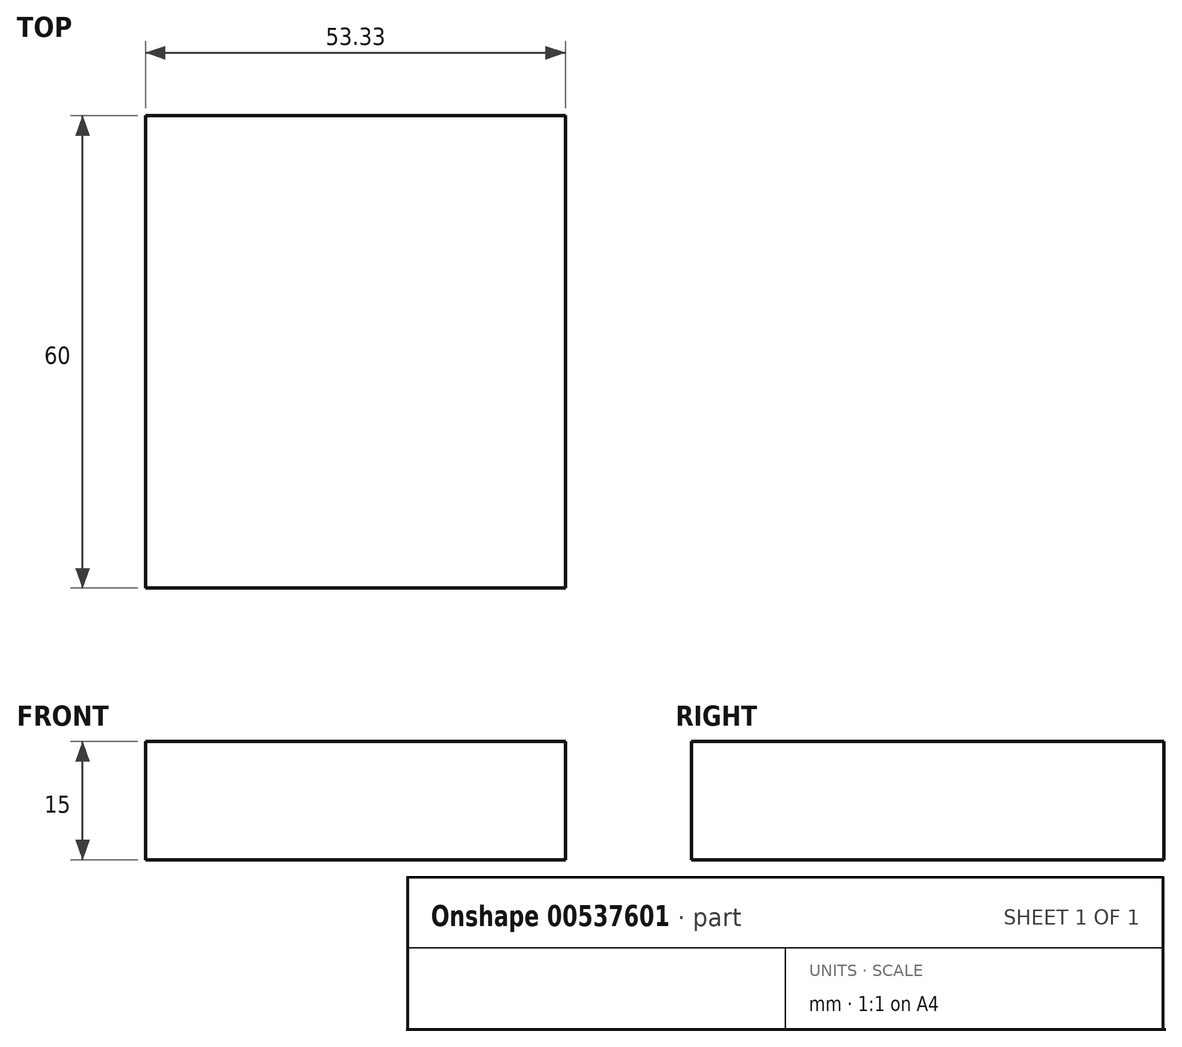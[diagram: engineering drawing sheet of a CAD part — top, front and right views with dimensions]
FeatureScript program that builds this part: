
annotation { "Feature Type Name" : "Feature", "Feature Type Description" : "" }
export const myFeature = defineFeature(function(context is Context, id is Id, definition is map)
    precondition{}
    {
        {
            var Q0;
            Q0=qCreatedBy(makeId("Top.planeOp"),FACE);
            var sketch = newSketch(context, id + "F0", { "sketchPlane" : qUnion([Q0])});
            skLineSegment(sketch, "E0.bottom", {"start": v(0, 0) * mm, "end": v(53.33, 0) * mm});
            skLineSegment(sketch, "E0.top", {"start": v(0, -60) * mm, "end": v(53.33, -60) * mm});
            skLineSegment(sketch, "E0.left", {"start": v(0, 0) * mm, "end": v(0, -60) * mm});
            skLineSegment(sketch, "E0.right", {"start": v(53.33, 0) * mm, "end": v(53.33, -60) * mm});
            skSolve(sketch);
        }
        {
            var Q0;
            Q0 = qSketchRegion(id + "F0", true);
            extrude(context, id + "F1", {"entities" : qUnion([Q0]), "depth" : 15 * mm, "offsetDistance" : 25 * mm});
        }
    });
